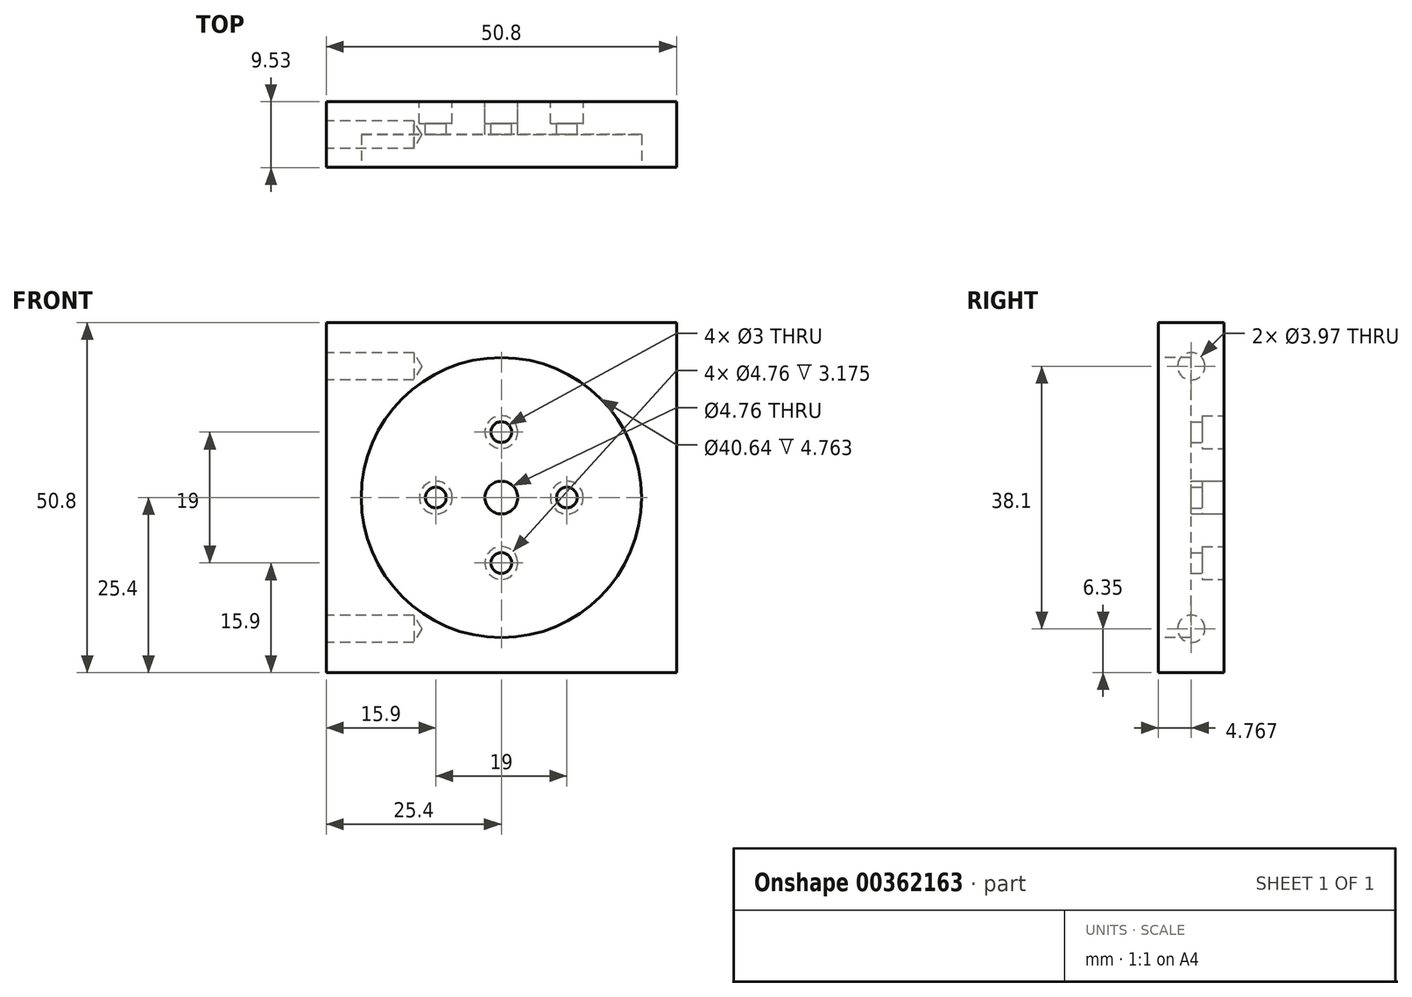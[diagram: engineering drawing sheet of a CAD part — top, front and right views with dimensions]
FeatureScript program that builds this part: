
annotation { "Feature Type Name" : "Feature", "Feature Type Description" : "" }
export const myFeature = defineFeature(function(context is Context, id is Id, definition is map)
    precondition{}
    {
        {
            var Q0;
            Q0=qCreatedBy(makeId("Front.planeOp"),FACE);
            var sketch = newSketch(context, id + "F0", { "sketchPlane" : qUnion([Q0])});
            skLineSegment(sketch, "E0.bottom", {"start": v(0, 0) * mm, "end": v(50.8, 0) * mm});
            skLineSegment(sketch, "E0.top", {"start": v(0, 50.8) * mm, "end": v(50.8, 50.8) * mm});
            skLineSegment(sketch, "E0.left", {"start": v(0, 0) * mm, "end": v(0, 50.8) * mm});
            skLineSegment(sketch, "E0.right", {"start": v(50.8, 0) * mm, "end": v(50.8, 50.8) * mm});
            skLineSegment(sketch, "E1", {"start": v(50.8, 25.4) * mm, "end": v(0, 25.4) * mm, "construction": true});
            skPoint(sketch, "E2", {"position": v(25.4, 25.4) * mm});
            skLineSegment(sketch, "E3", {"start": v(25.4, 25.4) * mm, "end": v(25.4, 34.9) * mm, "construction": true});
            skLineSegment(sketch, "E4", {"start": v(25.4, 25.4) * mm, "end": v(25.4, 15.9) * mm, "construction": true});
            skLineSegment(sketch, "E5", {"start": v(25.4, 34.9) * mm, "end": v(15.9, 34.9) * mm, "construction": true});
            skLineSegment(sketch, "E6", {"start": v(15.9, 34.9) * mm, "end": v(15.9, 25.4) * mm, "construction": true});
            skLineSegment(sketch, "E7", {"start": v(15.9, 25.4) * mm, "end": v(15.9, 15.9) * mm, "construction": true});
            skLineSegment(sketch, "E8", {"start": v(15.9, 15.9) * mm, "end": v(25.4, 15.9) * mm, "construction": true});
            skLineSegment(sketch, "E9", {"start": v(34.9, 15.9) * mm, "end": v(34.9, 25.4) * mm, "construction": true});
            skLineSegment(sketch, "E10", {"start": v(34.9, 25.4) * mm, "end": v(34.9, 34.9) * mm, "construction": true});
            skLineSegment(sketch, "E11", {"start": v(34.9, 34.9) * mm, "end": v(25.4, 34.9) * mm, "construction": true});
            skLineSegment(sketch, "E12", {"start": v(34.9, 15.9) * mm, "end": v(25.4, 15.9) * mm, "construction": true});
            skPoint(sketch, "E13", {"position": v(15.9, 25.4) * mm});
            skPoint(sketch, "E14", {"position": v(34.9, 25.4) * mm});
            skPoint(sketch, "E15", {"position": v(25.4, 34.9) * mm});
            skPoint(sketch, "E16", {"position": v(25.4, 15.9) * mm});
            skSolve(sketch);
        }
        {
            var Q0;
            Q0=makeQuery(id+"F0.imprint","IMPRINT",FACE,{"disambiguationData":[TD([[makeQuery(id+"F0.imprint","IMPRINT",EDGE,{"derivedFrom":sQuery(id+"F0.wireOp",EDGE,"E0.bottom")}),1.0]])]});
            extrude(context, id + "F1", {"entities" : qUnion([Q0]), "depth" : 9.52 * mm});
        }
        {
            var Q0;
            Q0=makeQuery(id+"F1.opExtrude","SWEPT_FACE",FACE,{"disambiguationData":[OSD([sQuery(id+"F0.wireOp",EDGE,"E0.left")])]});
            var sketch = newSketch(context, id + "F2", { "sketchPlane" : qUnion([Q0])});
            skLineSegment(sketch, "E17.0", {"start": v(9.53, 50.8) * mm, "end": v(0, 50.8) * mm});
            skLineSegment(sketch, "E18.0", {"start": v(9.53, 0) * mm, "end": v(9.53, 50.8) * mm});
            skLineSegment(sketch, "E19.0", {"start": v(0, 0) * mm, "end": v(0, 50.8) * mm});
            skPoint(sketch, "E20.0", {"position": v(4.76, 0) * mm});
            skLineSegment(sketch, "E21.0", {"start": v(9.53, 0) * mm, "end": v(0, 0) * mm});
            skPoint(sketch, "E22", {"position": v(4.76, 12.7) * mm});
            skLineSegment(sketch, "E23", {"start": v(9.53, 38.1) * mm, "end": v(0, 38.1) * mm, "construction": true});
            skLineSegment(sketch, "E24", {"start": v(9.53, 12.7) * mm, "end": v(0, 12.7) * mm, "construction": true});
            skLineSegment(sketch, "E25", {"start": v(4.76, 12.7) * mm, "end": v(4.76, 0) * mm, "construction": true});
            skLineSegment(sketch, "E26", {"start": v(4.76, 38.1) * mm, "end": v(4.76, 50.8) * mm, "construction": true});
            skLineSegment(sketch, "E27", {"start": v(4.76, 38.1) * mm, "end": v(4.76, 25.4) * mm, "construction": true});
            skLineSegment(sketch, "E28", {"start": v(4.76, 25.4) * mm, "end": v(4.76, 12.7) * mm, "construction": true});
            skPoint(sketch, "E29", {"position": v(4.76, 25.4) * mm});
            skPoint(sketch, "E30", {"position": v(4.76, 38.1) * mm});
            skPoint(sketch, "E31", {"position": v(4.76, 44.45) * mm});
            skPoint(sketch, "E32", {"position": v(4.76, 6.35) * mm});
            skSolve(sketch);
        }
        {
            var Q0;
            Q0=sQuery(id+"F2.wireOp",VERTEX,"E31");
            var Q1;
            Q1=sQuery(id+"F2.wireOp",VERTEX,"E32");
            var Q2;
            Q2=makeQuery(id+"F1.opExtrude","SWEPT_BODY",BODY,{"disambiguationData":[OSD([sQuery(id+"F0.wireOp",EDGE,"E0.bottom"),sQuery(id+"F0.wireOp",EDGE,"E0.top"),sQuery(id+"F0.wireOp",EDGE,"E0.left"),sQuery(id+"F0.wireOp",EDGE,"E0.right")])]});
            hole(context, id + "F3", {"style" : HoleStyle.SIMPLE, "endStyle" : HoleEndStyle.BLIND, "holeDiameter" : 3.97 * mm, "holeDepth" : 12.7 * mm, "isTappedThrough" : true, "tappedDepth" : 12.7 * mm, "tapClearance" : 3, "startFromSketch" : true, "locations" : qUnion([Q0, Q1]), "scope" : qUnion([Q2])});
        }
        {
            var Q0;
            Q0=sQuery(id+"F0.wireOp",VERTEX,"E15");
            var Q1;
            Q1=sQuery(id+"F0.wireOp",VERTEX,"E13");
            var Q2;
            Q2=sQuery(id+"F0.wireOp",VERTEX,"E16");
            var Q3;
            Q3=sQuery(id+"F0.wireOp",VERTEX,"E14");
            var Q4;
            Q4=makeQuery(id+"F1.opExtrude","SWEPT_BODY",BODY,{"disambiguationData":[OSD([sQuery(id+"F0.wireOp",EDGE,"E0.bottom"),sQuery(id+"F0.wireOp",EDGE,"E0.top"),sQuery(id+"F0.wireOp",EDGE,"E0.left"),sQuery(id+"F0.wireOp",EDGE,"E0.right")])]});
            hole(context, id + "F4", {"style" : HoleStyle.C_BORE, "endStyle" : HoleEndStyle.THROUGH, "oppositeDirection" : true, "holeDiameter" : 3 * mm, "cBoreDiameter" : 4.76 * mm, "cBoreDepth" : 3.17 * mm, "isTappedThrough" : true, "tappedDepth" : 12.7 * mm, "tapClearance" : 3, "startFromSketch" : true, "locations" : qUnion([Q0, Q1, Q2, Q3]), "scope" : qUnion([Q4])});
        }
        {
            var Q0;
            Q0=sQuery(id+"F0.wireOp",VERTEX,"E4.start");
            var Q1;
            Q1=makeQuery(id+"F1.opExtrude","SWEPT_BODY",BODY,{"disambiguationData":[OSD([sQuery(id+"F0.wireOp",EDGE,"E0.bottom"),sQuery(id+"F0.wireOp",EDGE,"E0.top"),sQuery(id+"F0.wireOp",EDGE,"E0.left"),sQuery(id+"F0.wireOp",EDGE,"E0.right")])]});
            hole(context, id + "F5", {"style" : HoleStyle.SIMPLE, "endStyle" : HoleEndStyle.BLIND, "oppositeDirection" : true, "holeDiameter" : 4.76 * mm, "holeDepth" : 12.7 * mm, "isTappedThrough" : true, "tappedDepth" : 12.7 * mm, "tapClearance" : 3, "startFromSketch" : true, "locations" : qUnion([Q0]), "scope" : qUnion([Q1])});
        }
        {
            var Q0;
            Q0=makeQuery(id+"F1.opExtrude","CAP_FACE",FACE,{"disambiguationData":[OSD([sQuery(id+"F0.wireOp",EDGE,"E0.bottom"),sQuery(id+"F0.wireOp",EDGE,"E0.top"),sQuery(id+"F0.wireOp",EDGE,"E0.left"),sQuery(id+"F0.wireOp",EDGE,"E0.right")])],"isStart":false});
            var sketch = newSketch(context, id + "F6", { "sketchPlane" : qUnion([Q0])});
            skCircle(sketch, "E33", {"center": v(25.4, 25.4) * mm, "radius": 20.32 * mm});
            skSolve(sketch);
        }
        {
            var Q0;
            Q0=makeQuery(id+"F6.imprint","IMPRINT",FACE,{"disambiguationData":[TD([[makeQuery(id+"F6.imprint","IMPRINT",EDGE,{"derivedFrom":sQuery(id+"F6.wireOp",EDGE,"E33")}),1.0]])]});
            extrude(context, id + "F7", {"entities" : qUnion([Q0]), "operationType" : NewBodyOperationType.REMOVE, "oppositeDirection" : true, "depth" : 4.76 * mm});
        }
    });
